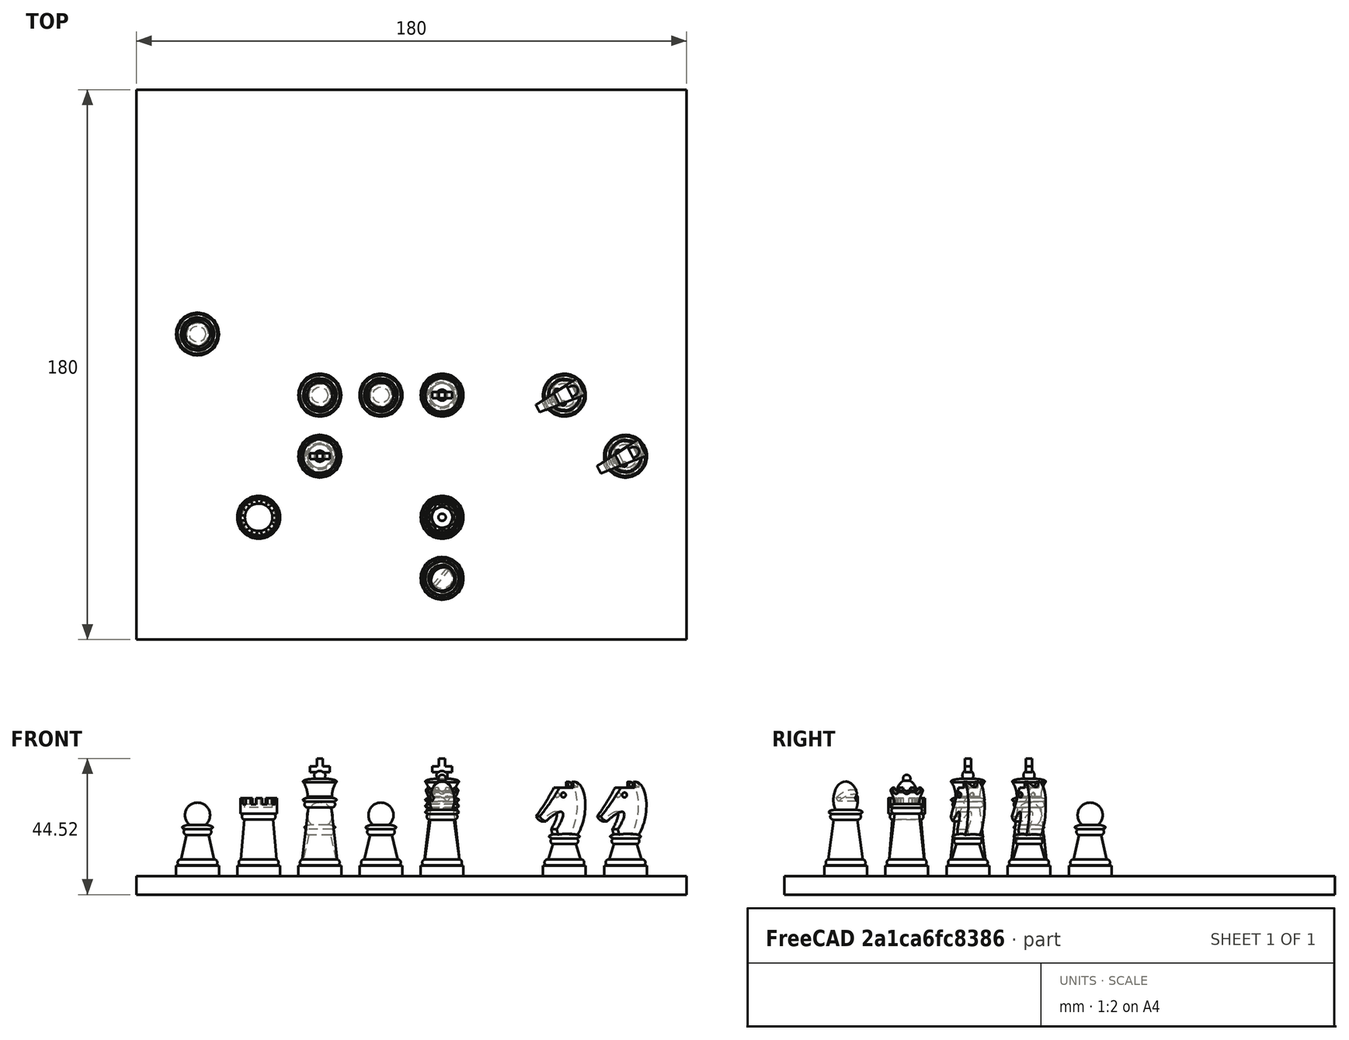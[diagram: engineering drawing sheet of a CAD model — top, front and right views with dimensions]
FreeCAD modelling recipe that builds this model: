
FCSTD DOCUMENT  (FreeCAD 0.18.4R)
Label: Chess
License: All rights reserved
LicenseURL: http://de.wikipedia.org/wiki/Alle_Rechte_vorbehalten
objects: Part::Cut×31, Part::MultiFuse×27, Part::Ellipsoid×24, Part::Torus×23, Part::Cylinder×20, Part::Box×19, Part::Cone×13, Part::Sphere×11, Part::MultiCommon×2, Part::FeaturePython×2, Part::Plane×1
note: 173 computed .brp shape members not serialized (recipe doc carries the construction recipe); baked Part::Feature solids carry a one-line shape summary decoded from their .brp

FEATURE [Part::Cylinder] Cylinder  label="Zylinder"
  Angle = 360
  AttacherType = Attacher::AttachEngine3D
  Height = 3.5
  Radius = 7
FEATURE [Part::Cone] Cone  label="Kegel"
  Angle = 360
  AttacherType = Attacher::AttachEngine3D
  Height = 18
  Placement = pos=(0,0,3) rot=(0,0,1;0rad)
  Radius1 = 6
  Radius2 = 4.5
FEATURE [Part::Cylinder] Cylinder001  label="Zylinder001"
  Angle = 360
  AttacherType = Attacher::AttachEngine3D
  Height = 5
  Placement = pos=(0,0,20.5) rot=(0,0,1;0rad)
  Radius = 6
FEATURE [Part::Torus] Torus
  Angle1 = -180
  Angle2 = 180
  Angle3 = 360
  AttacherType = Attacher::AttachEngine3D
  Placement = pos=(0,0,4.5) rot=(0,0,1;0rad)
  Radius1 = 5.5
  Radius2 = 1
FEATURE [Part::Torus] Torus001
  Angle1 = -180
  Angle2 = 180
  Angle3 = 360
  AttacherType = Attacher::AttachEngine3D
  Placement = pos=(0,0,19.5) rot=(0,0,1;0rad)
  Radius1 = 4.5
  Radius2 = 1
FEATURE [Part::Cylinder] Cylinder002  label="Zylinder002"
  Angle = 360
  AttacherType = Attacher::AttachEngine3D
  Height = 10
  Placement = pos=(0,0,22.5) rot=(0,0,1;0rad)
  Radius = 4.5
FEATURE [Part::Cut] Cut
  Base = -> Cylinder001
  Tool = -> Cylinder002
FEATURE [Part::Box] Box  label="Quader"
  AttacherType = Attacher::AttachEngine3D
  Height = 4
  Length = 14
  Placement = pos=(-7,-1,23.5) rot=(0,0,1;0rad)
  Width = 1.7
FEATURE [Part::Box] Box001  label="Quader001"
  AttacherType = Attacher::AttachEngine3D
  Height = 4
  Length = 14
  Placement = pos=(-5.07533,-4.92351,23.5) rot=(0,0,1;0.628319rad)
  Width = 1.7
FEATURE [Part::Box] Box002  label="Quader002"
  AttacherType = Attacher::AttachEngine3D
  Height = 4
  Length = 14
  Placement = pos=(-1.21206,-6.96641,23.5) rot=(0,0,1;1.25664rad)
  Width = 1.7
FEATURE [Part::Box] Box003  label="Quader003"
  AttacherType = Attacher::AttachEngine3D
  Height = 4
  Length = 14
  Placement = pos=(3.11418,-6.34838,23.5) rot=(0,0,1;1.88496rad)
  Width = 1.7
FEATURE [Part::Box] Box004  label="Quader004"
  AttacherType = Attacher::AttachEngine3D
  Height = 4
  Length = 14
  Placement = pos=(6.2509,-3.30548,23.5) rot=(0,0,1;2.51327rad)
  Width = 1.7
FEATURE [Part::Cut] Cut001
  Base = -> Cut
  Tool = -> Box
FEATURE [Part::Cut] Cut002
  Base = -> Cut001
  Tool = -> Box001
FEATURE [Part::Cut] Cut003
  Base = -> Cut002
  Tool = -> Box002
FEATURE [Part::Cut] Cut004
  Base = -> Cut003
  Tool = -> Box003
FEATURE [Part::Cut] Cut005
  Base = -> Cut004
  Tool = -> Box004
FEATURE [Part::MultiFuse] Fusion
  Shapes = -> [Cone,Cut005]
FEATURE [Part::MultiFuse] Fusion001
  Shapes = -> [Cylinder,Fusion]
FEATURE [Part::MultiFuse] Fusion002
  Shapes = -> [Torus001,Fusion001]
FEATURE [Part::MultiFuse] Fusion003  label="Rook_B2"
  Placement = pos=(20,20,0) rot=(0,0,1;0rad)
  Shapes = -> [Torus,Fusion002]
FEATURE [Part::Cylinder] Cylinder003  label="Zylinder003"
  Angle = 360
  AttacherType = Attacher::AttachEngine3D
  Height = 3.5
  Radius = 7
FEATURE [Part::Cone] Cone001  label="Kegel001"
  Angle = 360
  AttacherType = Attacher::AttachEngine3D
  Height = 18
  Placement = pos=(0,0,3) rot=(0,0,1;0rad)
  Radius1 = 6
  Radius2 = 3.5
FEATURE [Part::Torus] Torus002
  Angle1 = -180
  Angle2 = 180
  Angle3 = 360
  AttacherType = Attacher::AttachEngine3D
  Placement = pos=(0,0,4.5) rot=(0,0,1;0rad)
  Radius1 = 5.5
  Radius2 = 1
FEATURE [Part::Torus] Torus003
  Angle1 = -180
  Angle2 = 180
  Angle3 = 360
  AttacherType = Attacher::AttachEngine3D
  Placement = pos=(0,0,19.5) rot=(0,0,1;0rad)
  Radius1 = 4
  Radius2 = 1
FEATURE [Part::Ellipsoid] Ellipsoid001
  Angle1 = -90
  Angle2 = 90
  Angle3 = 360
  AttacherType = Attacher::AttachEngine3D
  Placement = pos=(0,0,25) rot=(0,0,1;0rad)
  Radius1 = 6
  Radius2 = 4
  Radius3 = 4
FEATURE [Part::Ellipsoid] Ellipsoid
  Angle1 = -90
  Angle2 = 90
  Angle3 = 360
  AttacherType = Attacher::AttachEngine3D
  Placement = pos=(0,0,21) rot=(0,0,1;0rad)
  Radius1 = 1
  Radius2 = 5.5
  Radius3 = 5.5
FEATURE [Part::MultiFuse] Fusion004
  Shapes = -> [Cylinder003,Cone001]
FEATURE [Part::MultiFuse] Fusion005
  Shapes = -> [Fusion004,Torus003]
FEATURE [Part::MultiFuse] Fusion006
  Shapes = -> [Fusion005,Torus002]
FEATURE [Part::MultiFuse] Fusion007
  Shapes = -> [Fusion006,Ellipsoid]
FEATURE [Part::MultiFuse] Fusion008
  Shapes = -> [Fusion007,Ellipsoid001]
FEATURE [Part::Box] Box009  label="Quader005"
  AttacherType = Attacher::AttachEngine3D
  Height = 1.5
  Length = 10
  Placement = pos=(1,-5,24.5) rot=(0,-1,0;0.698132rad)
  Width = 10
FEATURE [Part::Cut] Cut006  label="Bishop_E1"
  Base = -> Fusion008
  Placement = pos=(80,0,0) rot=(0,0,1;2.44346rad)
  Tool = -> Box009
FEATURE [Part::Plane] Plane  label="Board"
  AttacherType = Attacher::AttachEngine3D
  Length = 160
  Placement = pos=(-10,-10,0.01) rot=(0,0,1;0rad)
  Width = 160
FEATURE [Part::Torus] Torus004
  Angle1 = -180
  Angle2 = 180
  Angle3 = 360
  AttacherType = Attacher::AttachEngine3D
  Placement = pos=(0,0,4.5) rot=(0,0,1;0rad)
  Radius1 = 5.5
  Radius2 = 1
FEATURE [Part::Cylinder] Cylinder004  label="Zylinder004"
  Angle = 360
  AttacherType = Attacher::AttachEngine3D
  Height = 3.5
  Radius = 7
FEATURE [Part::Ellipsoid] Ellipsoid002
  Angle1 = -90
  Angle2 = 90
  Angle3 = 360
  AttacherType = Attacher::AttachEngine3D
  Placement = pos=(0,0,25) rot=(0,0,1;0rad)
  Radius1 = 1
  Radius2 = 5.5
  Radius3 = 5.5
FEATURE [Part::Torus] Torus005
  Angle1 = -180
  Angle2 = 180
  Angle3 = 360
  AttacherType = Attacher::AttachEngine3D
  Placement = pos=(0,0,23.5) rot=(0,0,1;0rad)
  Radius1 = 4
  Radius2 = 1
FEATURE [Part::Cone] Cone002  label="Kegel002"
  Angle = 360
  AttacherType = Attacher::AttachEngine3D
  Height = 22
  Placement = pos=(0,0,3) rot=(0,0,1;0rad)
  Radius1 = 6
  Radius2 = 3.5
FEATURE [Part::Ellipsoid] Ellipsoid003
  Angle1 = -90
  Angle2 = 90
  Angle3 = 360
  AttacherType = Attacher::AttachEngine3D
  Placement = pos=(0,0,31) rot=(0,0,1;0rad)
  Radius1 = 1
  Radius2 = 5.5
  Radius3 = 5.5
FEATURE [Part::Cone] Cone003  label="Kegel003"
  Angle = 360
  AttacherType = Attacher::AttachEngine3D
  Height = 9
  Placement = pos=(0,0,22) rot=(0,0,1;0rad)
  Radius1 = 2.8
  Radius2 = 5.5
FEATURE [Part::Torus] Torus006
  Angle1 = -180
  Angle2 = 180
  Angle3 = 360
  AttacherType = Attacher::AttachEngine3D
  Placement = pos=(0,0,26.3) rot=(0,0,1;0rad)
  Radius1 = 12
  Radius2 = 8
FEATURE [Part::Cut] Cut007
  Base = -> Cone003
  Tool = -> Torus006
FEATURE [Part::Sphere] Sphere  label="Kugel"
  Angle1 = -90
  Angle2 = 90
  Angle3 = 360
  AttacherType = Attacher::AttachEngine3D
  Placement = pos=(0,0,33) rot=(0,0,1;0rad)
  Radius = 1.8
FEATURE [Part::Box] Box010  label="Würfel"
  AttacherType = Attacher::AttachEngine3D
  Height = 5.5
  Length = 2
  Placement = pos=(-1,-1,33) rot=(0,0,1;0rad)
  Width = 2
FEATURE [Part::Box] Box011  label="Würfel001"
  AttacherType = Attacher::AttachEngine3D
  Height = 2
  Length = 6.4
  Placement = pos=(-3.2,-1,34) rot=(0,0,1;0rad)
  Width = 2
FEATURE [Part::MultiFuse] Fusion009  label="King_E4"
  Placement = pos=(80,60,0) rot=(0,0,1;0rad)
  Shapes = -> [Torus004,Cone002,Torus005,Box011,Box010,Ellipsoid003,Cylinder004,Ellipsoid002,Sphere,Cut007]
FEATURE [Part::Torus] Torus007
  Angle1 = -180
  Angle2 = 180
  Angle3 = 360
  AttacherType = Attacher::AttachEngine3D
  Placement = pos=(0,0,4.5) rot=(0,0,1;0rad)
  Radius1 = 5.5
  Radius2 = 1
FEATURE [Part::Cylinder] Cylinder005  label="Zylinder005"
  Angle = 360
  AttacherType = Attacher::AttachEngine3D
  Height = 3.5
  Radius = 7
FEATURE [Part::Cone] Cone004  label="Kegel004"
  Angle = 360
  AttacherType = Attacher::AttachEngine3D
  Height = 13
  Placement = pos=(0,0,3) rot=(0,0,1;0rad)
  Radius1 = 6
  Radius2 = 3
FEATURE [Part::Ellipsoid] Ellipsoid004
  Angle1 = -90
  Angle2 = 90
  Angle3 = 360
  AttacherType = Attacher::AttachEngine3D
  Placement = pos=(0,0,16) rot=(0,0,1;0rad)
  Radius1 = 1
  Radius2 = 5
  Radius3 = 5
FEATURE [Part::Torus] Torus008
  Angle1 = -180
  Angle2 = 180
  Angle3 = 360
  AttacherType = Attacher::AttachEngine3D
  Placement = pos=(0,0,14.5) rot=(0,0,1;0rad)
  Radius1 = 3.5
  Radius2 = 1
FEATURE [Part::Sphere] Sphere001  label="Kugel001"
  Angle1 = -90
  Angle2 = 90
  Angle3 = 360
  AttacherType = Attacher::AttachEngine3D
  Placement = pos=(0,0,20) rot=(0,0,1;0rad)
  Radius = 4.1
FEATURE [Part::MultiFuse] Fusion010  label="Pawn_D4"
  Placement = pos=(60,60,0) rot=(0,0,1;0rad)
  Shapes = -> [Torus007,Sphere001,Cylinder005,Torus008,Ellipsoid004,Cone004]
FEATURE [Part::Torus] Torus009
  Angle1 = -180
  Angle2 = 180
  Angle3 = 360
  AttacherType = Attacher::AttachEngine3D
  Placement = pos=(0,0,4.5) rot=(0,0,1;0rad)
  Radius1 = 5.5
  Radius2 = 1
FEATURE [Part::Cone] Cone005  label="Kegel005"
  Angle = 360
  AttacherType = Attacher::AttachEngine3D
  Height = 22
  Placement = pos=(0,0,3) rot=(0,0,1;0rad)
  Radius1 = 6
  Radius2 = 3.5
FEATURE [Part::Torus] Torus010
  Angle1 = -180
  Angle2 = 180
  Angle3 = 360
  AttacherType = Attacher::AttachEngine3D
  Placement = pos=(0,0,21.5) rot=(0,0,1;0rad)
  Radius1 = 4
  Radius2 = 1
FEATURE [Part::Cylinder] Cylinder006  label="Zylinder006"
  Angle = 360
  AttacherType = Attacher::AttachEngine3D
  Height = 3.5
  Radius = 7
FEATURE [Part::Ellipsoid] Ellipsoid005
  Angle1 = -90
  Angle2 = 90
  Angle3 = 360
  AttacherType = Attacher::AttachEngine3D
  Placement = pos=(0,0,23) rot=(0,0,1;0rad)
  Radius1 = 1
  Radius2 = 5.5
  Radius3 = 5.5
FEATURE [Part::Sphere] Sphere002  label="Kugel002"
  Angle1 = -90
  Angle2 = 90
  Angle3 = 360
  AttacherType = Attacher::AttachEngine3D
  Placement = pos=(0,0,32) rot=(0,0,1;0rad)
  Radius = 1.2
FEATURE [Part::Ellipsoid] Ellipsoid006
  Angle1 = -90
  Angle2 = 90
  Angle3 = 360
  AttacherType = Attacher::AttachEngine3D
  Placement = pos=(0,0,28) rot=(0,0,1;0rad)
  Radius1 = 2
  Radius2 = 5.4
  Radius3 = 5.4
FEATURE [Part::Cone] Cone006  label="Kegel006"
  Angle = 360
  AttacherType = Attacher::AttachEngine3D
  Height = 9
  Placement = pos=(0,0,19) rot=(0,0,1;0rad)
  Radius1 = 2.8
  Radius2 = 5.4
FEATURE [Part::Torus] Torus011
  Angle1 = -180
  Angle2 = 180
  Angle3 = 360
  AttacherType = Attacher::AttachEngine3D
  Placement = pos=(0,0,23.3) rot=(0,0,1;0rad)
  Radius1 = 12
  Radius2 = 8
FEATURE [Part::Cut] Cut008
  Base = -> Cone006
  Tool = -> Torus011
FEATURE [Part::Sphere] Sphere003  label="Kugel003"
  Angle1 = -90
  Angle2 = 90
  Angle3 = 360
  AttacherType = Attacher::AttachEngine3D
  Placement = pos=(0,0,31) rot=(0,0,1;0rad)
  Radius = 5
FEATURE [Part::MultiFuse] Fusion011
  Shapes = -> [Cut008,Ellipsoid006]
FEATURE [Part::Cut] Cut009
  Base = -> Fusion011
  Tool = -> Sphere003
FEATURE [Part::Ellipsoid] Ellipsoid007
  Angle1 = -90
  Angle2 = 90
  Angle3 = 360
  AttacherType = Attacher::AttachEngine3D
  Placement = pos=(0,0,26) rot=(0,0,1;0rad)
  Radius1 = 5.5
  Radius2 = 3.5
  Radius3 = 3.5
FEATURE [Part::MultiFuse] Fusion012
  Shapes = -> [Torus009,Cone005,Sphere002,Torus010,Ellipsoid005,Cylinder006,Ellipsoid007]
FEATURE [Part::Cylinder] Cylinder007  label="Zylinder007"
  Angle = 360
  AttacherType = Attacher::AttachEngine3D
  Height = 6
  Placement = pos=(7,0,26.5) rot=(0,-1,0;0.785398rad)
  Radius = 1.2
FEATURE [Part::Cylinder] Cylinder008  label="Zylinder008"
  Angle = 360
  AttacherType = Attacher::AttachEngine3D
  Height = 6
  Placement = pos=(4.94975,4.94975,26.5) rot=(0.281085,-0.678598,0.678598;1.09606rad)
  Radius = 1.2
FEATURE [Part::Cylinder] Cylinder009  label="Zylinder009"
  Angle = 360
  AttacherType = Attacher::AttachEngine3D
  Height = 6
  Placement = pos=(2e-15,7,26.5) rot=(0.357407,-0.357407,0.862856;1.71777rad)
  Radius = 1.2
FEATURE [Part::Cylinder] Cylinder010  label="Zylinder010"
  Angle = 360
  AttacherType = Attacher::AttachEngine3D
  Height = 6
  Placement = pos=(-4.94975,4.94975,26.5) rot=(0.377964,-0.156558,0.912487;2.41886rad)
  Radius = 1.2
FEATURE [Part::Cylinder] Cylinder011  label="Zylinder011"
  Angle = 360
  AttacherType = Attacher::AttachEngine3D
  Height = 6
  Placement = pos=(-7,1e-15,26.5) rot=(0.382683,0,0.92388;3.14159rad)
  Radius = 1.2
FEATURE [Part::Cylinder] Cylinder012  label="Zylinder012"
  Angle = 360
  AttacherType = Attacher::AttachEngine3D
  Height = 6
  Placement = pos=(-4.94975,-4.94975,26.5) rot=(0.377964,0.156558,0.912487;3.86433rad)
  Radius = 1.2
FEATURE [Part::Cylinder] Cylinder013  label="Zylinder013"
  Angle = 360
  AttacherType = Attacher::AttachEngine3D
  Height = 6
  Placement = pos=(-2e-15,-7,26.5) rot=(-0.357407,-0.357407,-0.862856;1.71777rad)
  Radius = 1.2
FEATURE [Part::Cylinder] Cylinder014  label="Zylinder014"
  Angle = 360
  AttacherType = Attacher::AttachEngine3D
  Height = 6
  Placement = pos=(4.94975,-4.94975,26.5) rot=(-0.281085,-0.678598,-0.678598;1.09606rad)
  Radius = 1.2
FEATURE [Part::Cut] Cut010
  Base = -> Cut009
  Tool = -> Cylinder007
FEATURE [Part::Cut] Cut011
  Base = -> Cut010
  Tool = -> Cylinder008
FEATURE [Part::Cut] Cut012
  Base = -> Cut011
  Tool = -> Cylinder009
FEATURE [Part::Cut] Cut013
  Base = -> Cut012
  Tool = -> Cylinder010
FEATURE [Part::Cut] Cut014
  Base = -> Cut013
  Tool = -> Cylinder011
FEATURE [Part::Cut] Cut015
  Base = -> Cut014
  Tool = -> Cylinder012
FEATURE [Part::Cut] Cut016
  Base = -> Cut015
  Tool = -> Cylinder013
FEATURE [Part::Cut] Cut017
  Base = -> Cut016
  Tool = -> Cylinder014
FEATURE [Part::MultiFuse] Fusion013  label="Queen_E2"
  Placement = pos=(80,20,0) rot=(0,0,1;0rad)
  Shapes = -> [Fusion012,Cut017]
FEATURE [Part::Cylinder] Cylinder015  label="Zylinder015"
  Angle = 360
  AttacherType = Attacher::AttachEngine3D
  Height = 3.5
  Radius = 7
FEATURE [Part::Cone] Cone007  label="Kegel007"
  Angle = 360
  AttacherType = Attacher::AttachEngine3D
  Height = 10
  Placement = pos=(0,0,3) rot=(0,0,1;0rad)
  Radius1 = 6
  Radius2 = 3
FEATURE [Part::Torus] Torus012
  Angle1 = -180
  Angle2 = 180
  Angle3 = 360
  AttacherType = Attacher::AttachEngine3D
  Placement = pos=(0,0,4.5) rot=(0,0,1;0rad)
  Radius1 = 5.5
  Radius2 = 1
FEATURE [Part::Torus] Torus013
  Angle1 = -180
  Angle2 = 180
  Angle3 = 360
  AttacherType = Attacher::AttachEngine3D
  Placement = pos=(0,0,11.5) rot=(0,0,1;0rad)
  Radius1 = 3.5
  Radius2 = 1
FEATURE [Part::Ellipsoid] Ellipsoid008
  Angle1 = -90
  Angle2 = 90
  Angle3 = 360
  AttacherType = Attacher::AttachEngine3D
  Placement = pos=(0,0,13) rot=(0,0,1;0rad)
  Radius1 = 1
  Radius2 = 5
  Radius3 = 5
FEATURE [Part::Ellipsoid] Ellipsoid009
  Angle1 = -90
  Angle2 = 90
  Angle3 = 360
  AttacherType = Attacher::AttachEngine3D
  Placement = pos=(1,0,21) rot=(0,1,0;0.15708rad)
  Radius1 = 10
  Radius2 = 5
  Radius3 = 40
FEATURE [Part::Box] Box012  label="Würfel002"
  AttacherType = Attacher::AttachEngine3D
  Height = 22
  Length = 22
  Placement = pos=(-13,-5,11) rot=(0,0,1;0rad)
  Width = 10
FEATURE [Part::Ellipsoid] Ellipsoid010  label="Ellipsoid013"
  Angle1 = -90
  Angle2 = 90
  Angle3 = 360
  AttacherType = Attacher::AttachEngine3D
  Placement = pos=(-3.5,0,24.5) rot=(0,1,0;0.785398rad)
  Radius1 = 8
  Radius2 = 5
  Radius3 = 40
FEATURE [Part::Ellipsoid] Ellipsoid011
  Angle1 = -90
  Angle2 = 90
  Angle3 = 360
  AttacherType = Attacher::AttachEngine3D
  Placement = pos=(-6.5,0,32.5) rot=(0,1,0;0.541052rad)
  Radius1 = 20
  Radius2 = 5
  Radius3 = 40
FEATURE [Part::Box] Box013  label="Würfel003"
  AttacherType = Attacher::AttachEngine3D
  Height = 10
  Length = 10
  Placement = pos=(-8,-3,29) rot=(0,0,1;0rad)
  Width = 6
FEATURE [Part::Ellipsoid] Ellipsoid012
  Angle1 = -90
  Angle2 = 90
  Angle3 = 360
  AttacherType = Attacher::AttachEngine3D
  Placement = pos=(-8.5,0,13.5) rot=(0,1,0;0.733038rad)
  Radius1 = 10
  Radius2 = 2.5
  Radius3 = 40
FEATURE [Part::MultiFuse] Fusion015
  Shapes = -> [Cylinder015,Torus013,Ellipsoid008,Cone007,Torus012]
FEATURE [Part::MultiFuse] Fusion016
  Shapes = -> [Ellipsoid010,Ellipsoid009]
FEATURE [Part::Cut] Cut018
  Base = -> Fusion016
  Tool = -> Ellipsoid011
FEATURE [Part::Cut] Cut019
  Base = -> Cut018
  Tool = -> Ellipsoid012
FEATURE [Part::Box] Box014  label="Würfel004"
  AttacherType = Attacher::AttachEngine3D
  Height = 22
  Length = 22
  Placement = pos=(-13,1,11) rot=(0,0,1;0.10472rad)
  Width = 4
FEATURE [Part::MultiCommon] Common
  Shapes = -> [Cut019,Box012]
FEATURE [Part::Box] Box015  label="Würfel005"
  AttacherType = Attacher::AttachEngine3D
  Height = 22
  Length = 22
  Placement = pos=(-13,-5,11) rot=(0,0,-1;0.10472rad)
  Width = 4
FEATURE [Part::Cut] Cut020
  Base = -> Common
  Tool = -> Box015
FEATURE [Part::Cut] Cut021
  Base = -> Cut020
  Tool = -> Box014
FEATURE [Part::Cut] Cut022
  Base = -> Cut021
  Tool = -> Box013
FEATURE [Part::Ellipsoid] Ellipsoid013  label="Ellipsoid014"
  Angle1 = -90
  Angle2 = 90
  Angle3 = 360
  AttacherType = Attacher::AttachEngine3D
  Placement = pos=(3,0,33) rot=(0,0,1;0rad)
  Radius1 = 4
  Radius2 = 6
  Radius3 = 2
FEATURE [Part::Cut] Cut023
  Base = -> Cut022
  Tool = -> Ellipsoid013
FEATURE [Part::Sphere] Sphere004  label="Kugel004"
  Angle1 = -90
  Angle2 = 90
  Angle3 = 360
  AttacherType = Attacher::AttachEngine3D
  Placement = pos=(-1.5,-2.2,26.6) rot=(0,0,1;0rad)
  Radius = 0.8
FEATURE [Part::Sphere] Sphere005  label="Kugel005"
  Angle1 = -90
  Angle2 = 90
  Angle3 = 360
  AttacherType = Attacher::AttachEngine3D
  Placement = pos=(-1.5,2.2,26.6) rot=(0,0,1;0rad)
  Radius = 0.8
FEATURE [Part::MultiFuse] Fusion017
  Shapes = -> [Cut023,Sphere004,Sphere005]
FEATURE [Part::MultiFuse] Fusion018  label="Knight_H3"
  Placement = pos=(140,40,0) rot=(0,0,1;0.471239rad)
  Shapes = -> [Fusion015,Fusion017]
FEATURE [Part::Torus] Torus014
  Angle1 = -180
  Angle2 = 180
  Angle3 = 360
  AttacherType = Attacher::AttachEngine3D
  Placement = pos=(0,0,4.5) rot=(0,0,1;0rad)
  Radius1 = 5.5
  Radius2 = 1
FEATURE [Part::Cylinder] Cylinder016  label="Zylinder016"
  Angle = 360
  AttacherType = Attacher::AttachEngine3D
  Height = 3.5
  Radius = 7
FEATURE [Part::Cone] Cone008  label="Kegel008"
  Angle = 360
  AttacherType = Attacher::AttachEngine3D
  Height = 13
  Placement = pos=(0,0,3) rot=(0,0,1;0rad)
  Radius1 = 6
  Radius2 = 3
FEATURE [Part::Ellipsoid] Ellipsoid014  label="Ellipsoid015"
  Angle1 = -90
  Angle2 = 90
  Angle3 = 360
  AttacherType = Attacher::AttachEngine3D
  Placement = pos=(0,0,16) rot=(0,0,1;0rad)
  Radius1 = 1
  Radius2 = 5
  Radius3 = 5
FEATURE [Part::Torus] Torus015
  Angle1 = -180
  Angle2 = 180
  Angle3 = 360
  AttacherType = Attacher::AttachEngine3D
  Placement = pos=(0,0,14.5) rot=(0,0,1;0rad)
  Radius1 = 3.5
  Radius2 = 1
FEATURE [Part::Sphere] Sphere007  label="Kugel007"
  Angle1 = -90
  Angle2 = 90
  Angle3 = 360
  AttacherType = Attacher::AttachEngine3D
  Placement = pos=(0,0,20) rot=(0,0,1;0rad)
  Radius = 4.1
FEATURE [Part::MultiFuse] Fusion021  label="Pawn_A5"
  Placement = pos=(0,80,0) rot=(0,0,1;0rad)
  Shapes = -> [Torus014,Sphere007,Cylinder016,Torus015,Ellipsoid014,Cone008]
FEATURE [Part::Torus] Torus016
  Angle1 = -180
  Angle2 = 180
  Angle3 = 360
  AttacherType = Attacher::AttachEngine3D
  Placement = pos=(0,0,4.5) rot=(0,0,1;0rad)
  Radius1 = 5.5
  Radius2 = 1
FEATURE [Part::Cylinder] Cylinder017  label="Zylinder017"
  Angle = 360
  AttacherType = Attacher::AttachEngine3D
  Height = 3.5
  Radius = 7
FEATURE [Part::Cone] Cone009  label="Kegel009"
  Angle = 360
  AttacherType = Attacher::AttachEngine3D
  Height = 13
  Placement = pos=(0,0,3) rot=(0,0,1;0rad)
  Radius1 = 6
  Radius2 = 3
FEATURE [Part::Ellipsoid] Ellipsoid015  label="Ellipsoid016"
  Angle1 = -90
  Angle2 = 90
  Angle3 = 360
  AttacherType = Attacher::AttachEngine3D
  Placement = pos=(0,0,16) rot=(0,0,1;0rad)
  Radius1 = 1
  Radius2 = 5
  Radius3 = 5
FEATURE [Part::Torus] Torus017
  Angle1 = -180
  Angle2 = 180
  Angle3 = 360
  AttacherType = Attacher::AttachEngine3D
  Placement = pos=(0,0,14.5) rot=(0,0,1;0rad)
  Radius1 = 3.5
  Radius2 = 1
FEATURE [Part::Sphere] Sphere008  label="Kugel008"
  Angle1 = -90
  Angle2 = 90
  Angle3 = 360
  AttacherType = Attacher::AttachEngine3D
  Placement = pos=(0,0,20) rot=(0,0,1;0rad)
  Radius = 4.1
FEATURE [Part::MultiFuse] Fusion022  label="Pawn_C4"
  Placement = pos=(40,60,0) rot=(0,0,1;0rad)
  Shapes = -> [Torus016,Sphere008,Cylinder017,Torus017,Ellipsoid015,Cone009]
FEATURE [Part::Cylinder] Cylinder018  label="Zylinder018"
  Angle = 360
  AttacherType = Attacher::AttachEngine3D
  Height = 3.5
  Radius = 7
FEATURE [Part::Torus] Torus018
  Angle1 = -180
  Angle2 = 180
  Angle3 = 360
  AttacherType = Attacher::AttachEngine3D
  Placement = pos=(0,0,4.5) rot=(0,0,1;0rad)
  Radius1 = 5.5
  Radius2 = 1
FEATURE [Part::Ellipsoid] Ellipsoid016  label="Ellipsoid017"
  Angle1 = -90
  Angle2 = 90
  Angle3 = 360
  AttacherType = Attacher::AttachEngine3D
  Placement = pos=(0,0,25) rot=(0,0,1;0rad)
  Radius1 = 1
  Radius2 = 5.5
  Radius3 = 5.5
FEATURE [Part::Torus] Torus019
  Angle1 = -180
  Angle2 = 180
  Angle3 = 360
  AttacherType = Attacher::AttachEngine3D
  Placement = pos=(0,0,23.5) rot=(0,0,1;0rad)
  Radius1 = 4
  Radius2 = 1
FEATURE [Part::Cone] Cone010  label="Kegel010"
  Angle = 360
  AttacherType = Attacher::AttachEngine3D
  Height = 22
  Placement = pos=(0,0,3) rot=(0,0,1;0rad)
  Radius1 = 6
  Radius2 = 3.5
FEATURE [Part::Ellipsoid] Ellipsoid017  label="Ellipsoid018"
  Angle1 = -90
  Angle2 = 90
  Angle3 = 360
  AttacherType = Attacher::AttachEngine3D
  Placement = pos=(0,0,31) rot=(0,0,1;0rad)
  Radius1 = 1
  Radius2 = 5.5
  Radius3 = 5.5
FEATURE [Part::Cone] Cone011  label="Kegel011"
  Angle = 360
  AttacherType = Attacher::AttachEngine3D
  Height = 9
  Placement = pos=(0,0,22) rot=(0,0,1;0rad)
  Radius1 = 2.8
  Radius2 = 5.5
FEATURE [Part::Torus] Torus020
  Angle1 = -180
  Angle2 = 180
  Angle3 = 360
  AttacherType = Attacher::AttachEngine3D
  Placement = pos=(0,0,26.3) rot=(0,0,1;0rad)
  Radius1 = 12
  Radius2 = 8
FEATURE [Part::Cut] Cut024
  Base = -> Cone011
  Tool = -> Torus020
FEATURE [Part::Sphere] Sphere009  label="Kugel009"
  Angle1 = -90
  Angle2 = 90
  Angle3 = 360
  AttacherType = Attacher::AttachEngine3D
  Placement = pos=(0,0,33) rot=(0,0,1;0rad)
  Radius = 1.8
FEATURE [Part::Box] Box016  label="Würfel006"
  AttacherType = Attacher::AttachEngine3D
  Height = 2
  Length = 6.4
  Placement = pos=(-3.2,-1,34) rot=(0,0,1;0rad)
  Width = 2
FEATURE [Part::Box] Box017  label="Würfel007"
  AttacherType = Attacher::AttachEngine3D
  Height = 5.5
  Length = 2
  Placement = pos=(-1,-1,33) rot=(0,0,1;0rad)
  Width = 2
FEATURE [Part::MultiFuse] Fusion023  label="King_C3"
  Placement = pos=(40,40,0) rot=(0,0,1;0rad)
  Shapes = -> [Torus018,Cone010,Torus019,Box016,Box017,Ellipsoid017,Cylinder018,Ellipsoid016,Sphere009,Cut024]
FEATURE [Part::Torus] Torus021
  Angle1 = -180
  Angle2 = 180
  Angle3 = 360
  AttacherType = Attacher::AttachEngine3D
  Placement = pos=(0,0,11.5) rot=(0,0,1;0rad)
  Radius1 = 3.5
  Radius2 = 1
FEATURE [Part::Ellipsoid] Ellipsoid018  label="Ellipsoid019"
  Angle1 = -90
  Angle2 = 90
  Angle3 = 360
  AttacherType = Attacher::AttachEngine3D
  Placement = pos=(1,0,21) rot=(0,1,0;0.15708rad)
  Radius1 = 10
  Radius2 = 5
  Radius3 = 40
FEATURE [Part::Ellipsoid] Ellipsoid019  label="Ellipsoid020"
  Angle1 = -90
  Angle2 = 90
  Angle3 = 360
  AttacherType = Attacher::AttachEngine3D
  Placement = pos=(-8.5,0,13.5) rot=(0,1,0;0.733038rad)
  Radius1 = 10
  Radius2 = 2.5
  Radius3 = 40
FEATURE [Part::Ellipsoid] Ellipsoid020  label="Ellipsoid021"
  Angle1 = -90
  Angle2 = 90
  Angle3 = 360
  AttacherType = Attacher::AttachEngine3D
  Placement = pos=(3,0,33) rot=(0,0,1;0rad)
  Radius1 = 4
  Radius2 = 6
  Radius3 = 2
FEATURE [Part::Box] Box018  label="Würfel008"
  AttacherType = Attacher::AttachEngine3D
  Height = 10
  Length = 10
  Placement = pos=(-8,-3,29) rot=(0,0,1;0rad)
  Width = 6
FEATURE [Part::Box] Box019  label="Würfel009"
  AttacherType = Attacher::AttachEngine3D
  Height = 22
  Length = 22
  Placement = pos=(-13,-5,11) rot=(0,0,-1;0.10472rad)
  Width = 4
FEATURE [Part::Ellipsoid] Ellipsoid021  label="Ellipsoid022"
  Angle1 = -90
  Angle2 = 90
  Angle3 = 360
  AttacherType = Attacher::AttachEngine3D
  Placement = pos=(0,0,13) rot=(0,0,1;0rad)
  Radius1 = 1
  Radius2 = 5
  Radius3 = 5
FEATURE [Part::Cylinder] Cylinder019  label="Zylinder019"
  Angle = 360
  AttacherType = Attacher::AttachEngine3D
  Height = 3.5
  Radius = 7
FEATURE [Part::Sphere] Sphere010  label="Kugel010"
  Angle1 = -90
  Angle2 = 90
  Angle3 = 360
  AttacherType = Attacher::AttachEngine3D
  Placement = pos=(-1.5,-2.2,26.6) rot=(0,0,1;0rad)
  Radius = 0.8
FEATURE [Part::Sphere] Sphere011  label="Kugel011"
  Angle1 = -90
  Angle2 = 90
  Angle3 = 360
  AttacherType = Attacher::AttachEngine3D
  Placement = pos=(-1.5,2.2,26.6) rot=(0,0,1;0rad)
  Radius = 0.8
FEATURE [Part::Cone] Cone012  label="Kegel012"
  Angle = 360
  AttacherType = Attacher::AttachEngine3D
  Height = 10
  Placement = pos=(0,0,3) rot=(0,0,1;0rad)
  Radius1 = 6
  Radius2 = 3
FEATURE [Part::Torus] Torus022
  Angle1 = -180
  Angle2 = 180
  Angle3 = 360
  AttacherType = Attacher::AttachEngine3D
  Placement = pos=(0,0,4.5) rot=(0,0,1;0rad)
  Radius1 = 5.5
  Radius2 = 1
FEATURE [Part::Ellipsoid] Ellipsoid022  label="Ellipsoid023"
  Angle1 = -90
  Angle2 = 90
  Angle3 = 360
  AttacherType = Attacher::AttachEngine3D
  Placement = pos=(-3.5,0,24.5) rot=(0,1,0;0.785398rad)
  Radius1 = 8
  Radius2 = 5
  Radius3 = 40
FEATURE [Part::Ellipsoid] Ellipsoid023  label="Ellipsoid024"
  Angle1 = -90
  Angle2 = 90
  Angle3 = 360
  AttacherType = Attacher::AttachEngine3D
  Placement = pos=(-6.5,0,32.5) rot=(0,1,0;0.541052rad)
  Radius1 = 20
  Radius2 = 5
  Radius3 = 40
FEATURE [Part::Box] Box020  label="Würfel010"
  AttacherType = Attacher::AttachEngine3D
  Height = 22
  Length = 22
  Placement = pos=(-13,-5,11) rot=(0,0,1;0rad)
  Width = 10
FEATURE [Part::MultiFuse] Fusion025
  Shapes = -> [Cylinder019,Torus021,Ellipsoid021,Cone012,Torus022]
FEATURE [Part::MultiFuse] Fusion026
  Shapes = -> [Ellipsoid022,Ellipsoid018]
FEATURE [Part::Box] Box021  label="Würfel011"
  AttacherType = Attacher::AttachEngine3D
  Height = 22
  Length = 22
  Placement = pos=(-13,1,11) rot=(0,0,1;0.10472rad)
  Width = 4
FEATURE [Part::Cut] Cut030
  Base = -> Fusion026
  Tool = -> Ellipsoid023
FEATURE [Part::Cut] Cut026
  Base = -> Cut030
  Tool = -> Ellipsoid019
FEATURE [Part::MultiCommon] Common001
  Shapes = -> [Cut026,Box020]
FEATURE [Part::Cut] Cut028
  Base = -> Common001
  Tool = -> Box019
FEATURE [Part::Cut] Cut027
  Base = -> Cut028
  Tool = -> Box021
FEATURE [Part::Cut] Cut029
  Base = -> Cut027
  Tool = -> Box018
FEATURE [Part::Cut] Cut025
  Base = -> Cut029
  Tool = -> Ellipsoid020
FEATURE [Part::MultiFuse] Fusion027
  Shapes = -> [Cut025,Sphere010,Sphere011]
FEATURE [Part::MultiFuse] Fusion024  label="Knight_G4"
  Placement = pos=(120,60,0) rot=(0,0,1;0.471239rad)
  Shapes = -> [Fusion025,Fusion027]
FEATURE [Part::MultiFuse] Fusion028  label="Black_pieces"
  Shapes = -> [Fusion021,Fusion022,Fusion010,Fusion023,Fusion024,Cut006]
FEATURE [Part::MultiFuse] Fusion029  label="White_pieces"
  Shapes = -> [Fusion018,Fusion003,Fusion009,Fusion013]
FEATURE [Part::Box] Box022  label="Frame"
  AttacherType = Attacher::AttachEngine3D
  Height = 6
  Length = 180
  Placement = pos=(-20,-20,-6.02) rot=(0,0,1;0rad)
  Width = 180
FEATURE [Part::FeaturePython] SpotLight  # WARN: FeaturePython — macro-defined, semantics opaque (R4)
  FadeDistance = 0
  FadePower = 0
  FallOff = 60
  Placement = pos=(80,60,100) rot=(1,0,0;1.5708rad)
  Radius = 60
  Tightness = 100
FEATURE [Part::FeaturePython] PointLight  # WARN: FeaturePython — macro-defined, semantics opaque (R4)
  FadeDistance = 0
  FadePower = 0
  Placement = pos=(100,-40,100) rot=(0,0,1;0rad)
